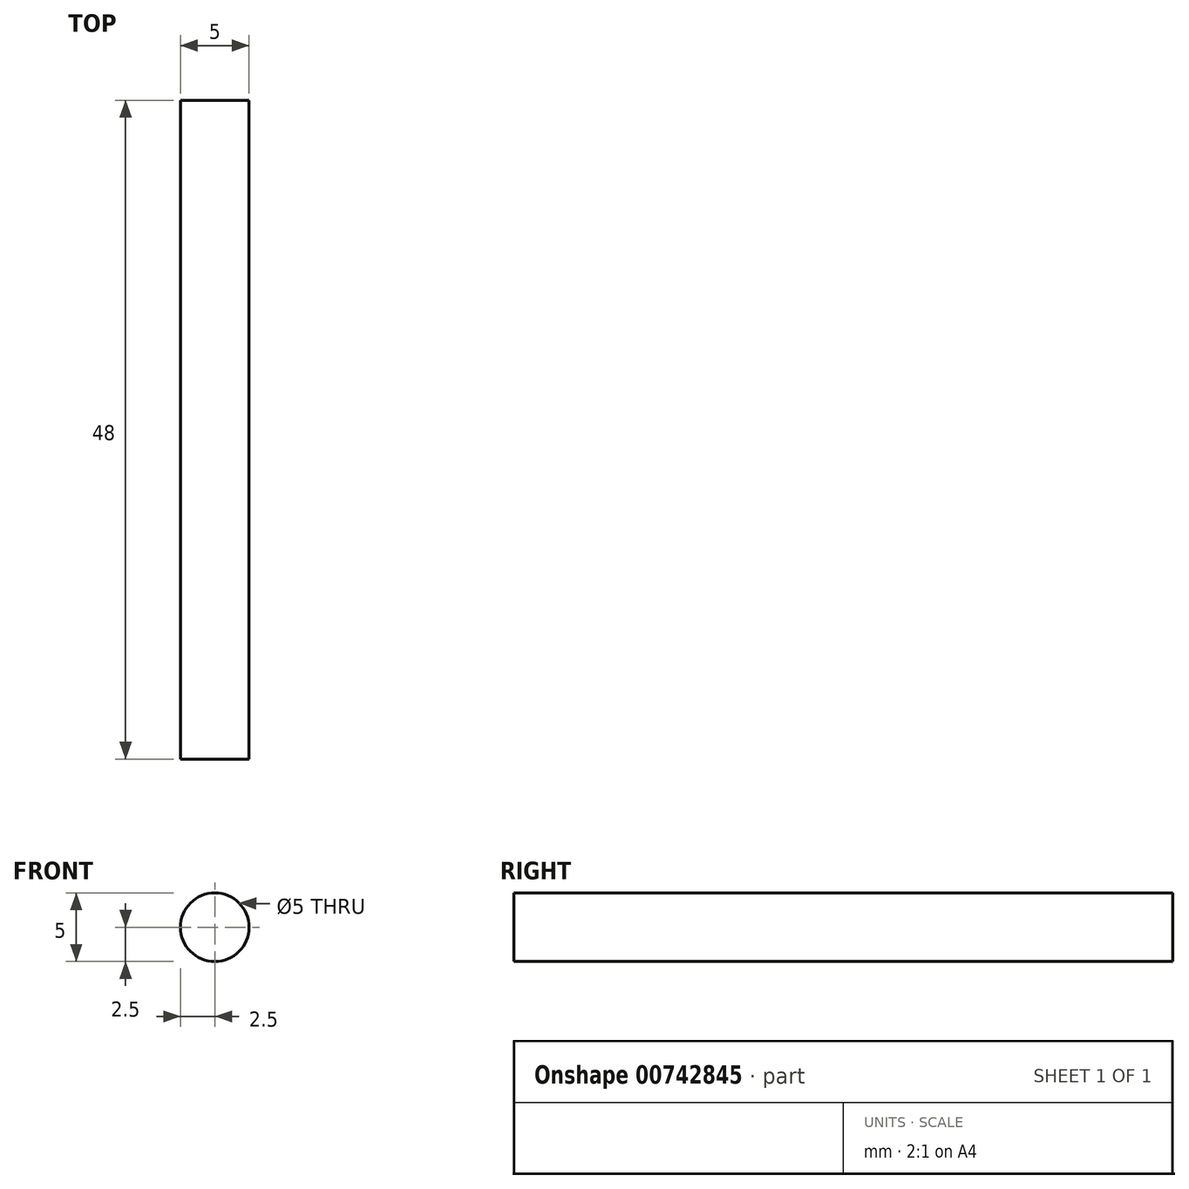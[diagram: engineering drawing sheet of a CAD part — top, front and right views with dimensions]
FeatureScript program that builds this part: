
annotation { "Feature Type Name" : "Feature", "Feature Type Description" : "" }
export const myFeature = defineFeature(function(context is Context, id is Id, definition is map)
    precondition{}
    {
        {
            var Q0;
            Q0=qCreatedBy(makeId("Front.planeOp"),FACE);
            var sketch = newSketch(context, id + "F0", { "sketchPlane" : qUnion([Q0])});
            skCircle(sketch, "E0", {"center": v(0, 0) * mm, "radius": 2.5 * mm});
            skSolve(sketch);
        }
        {
            var Q0;
            Q0=sQuery(id+"F0.wireOp",EDGE,"E0");
            extrude(context, id + "F1", {"bodyType" : ToolBodyType.SURFACE, "surfaceEntities" : qUnion([Q0]), "endBound" : BoundingType.SYMMETRIC, "oppositeDirection" : true, "depth" : 48 * mm, "offsetDistance" : 25 * mm});
        }
    });
